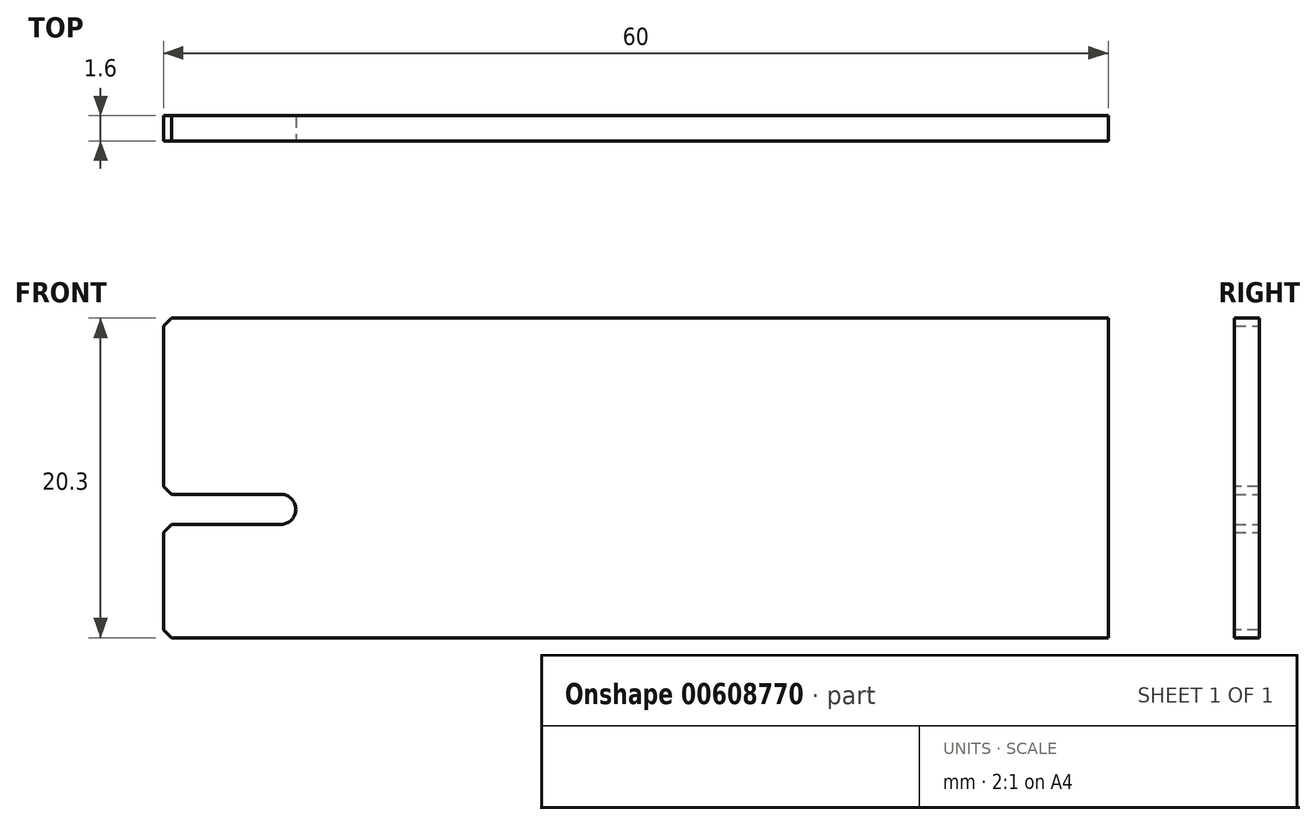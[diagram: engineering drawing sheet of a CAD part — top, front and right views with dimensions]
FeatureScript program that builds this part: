
annotation { "Feature Type Name" : "Feature", "Feature Type Description" : "" }
export const myFeature = defineFeature(function(context is Context, id is Id, definition is map)
    precondition{}
    {
        {
            var Q0;
            Q0=qCreatedBy(makeId("Front.planeOp"),FACE);
            var sketch = newSketch(context, id + "F0", { "sketchPlane" : qUnion([Q0])});
            skLineSegment(sketch, "E0.bottom", {"start": v(-10.18, 9.92) * mm, "end": v(49.82, 9.92) * mm});
            skLineSegment(sketch, "E0.top", {"start": v(-10.18, -10.38) * mm, "end": v(49.82, -10.38) * mm});
            skLineSegment(sketch, "E0.left", {"start": v(-10.18, 9.92) * mm, "end": v(-10.18, -10.38) * mm});
            skLineSegment(sketch, "E0.right", {"start": v(49.82, 9.92) * mm, "end": v(49.82, -10.38) * mm});
            skSolve(sketch);
        }
        {
            var Q0;
            Q0 = qSketchRegion(id + "F0", true);
            extrude(context, id + "F1", {"entities" : qUnion([Q0]), "depth" : 1.6 * mm, "offsetDistance" : 25 * mm});
        }
        {
            var Q0;
            Q0=qCreatedBy(makeId("Front.planeOp"),FACE);
            var sketch = newSketch(context, id + "F2", { "sketchPlane" : qUnion([Q0])});
            skLineSegment(sketch, "E1.bottom", {"start": v(-11.78, -1.28) * mm, "end": v(-1.78, -1.28) * mm});
            skLineSegment(sketch, "E1.top", {"start": v(-11.78, -3.18) * mm, "end": v(-1.78, -3.18) * mm});
            skLineSegment(sketch, "E1.left", {"start": v(-11.78, -1.28) * mm, "end": v(-11.78, -3.18) * mm});
            skLineSegment(sketch, "E1.right", {"start": v(-1.78, -1.28) * mm, "end": v(-1.78, -3.18) * mm});
            skSolve(sketch);
        }
        {
            var Q0;
            Q0 = qSketchRegion(id + "F2", true);
            extrude(context, id + "F3", {"entities" : qUnion([Q0]), "operationType" : NewBodyOperationType.REMOVE, "depth" : 25 * mm, "offsetDistance" : 25 * mm});
        }
        {
            var Q0;
            Q0=makeQuery(id+"F1.opExtrude","SWEPT_EDGE",EDGE,{"disambiguationData":[OSD([sQuery(id+"F0.wireOp",EDGE,"E0.bottom"),sQuery(id+"F0.wireOp",EDGE,"E0.left")])]});
            var Q1;
            Q1=makeQuery(id+"F3.boolean.opBoolean","INTERSECT",EDGE,{"derivedFrom":[makeQuery(id+"F1.opExtrude","SWEPT_FACE",FACE,{"disambiguationData":[OSD([sQuery(id+"F0.wireOp",EDGE,"E0.left")])]}),makeQuery(id+"F3.opExtrude","SWEPT_FACE",FACE,{"disambiguationData":[OSD([sQuery(id+"F2.wireOp",EDGE,"E1.bottom")])]})]});
            var Q2;
            Q2=makeQuery(id+"F3.boolean.opBoolean","INTERSECT",EDGE,{"derivedFrom":[makeQuery(id+"F1.opExtrude","SWEPT_FACE",FACE,{"disambiguationData":[OSD([sQuery(id+"F0.wireOp",EDGE,"E0.left")])]}),makeQuery(id+"F3.opExtrude","SWEPT_FACE",FACE,{"disambiguationData":[OSD([sQuery(id+"F2.wireOp",EDGE,"E1.top")])]})]});
            var Q3;
            Q3=makeQuery(id+"F1.opExtrude","SWEPT_EDGE",EDGE,{"disambiguationData":[OSD([sQuery(id+"F0.wireOp",EDGE,"E0.top"),sQuery(id+"F0.wireOp",EDGE,"E0.left")])]});
            chamfer(context, id + "F4", {"entities" : qUnion([Q0, Q1, Q2, Q3]), "width" : 0.5 * mm, "tangentPropagation" : true});
        }
        {
            var Q0;
            Q0=makeQuery(id+"F3.boolean.opBoolean","COPY",EDGE,{"derivedFrom":makeQuery(id+"F3.opExtrude","SWEPT_EDGE",EDGE,{"disambiguationData":[OSD([sQuery(id+"F2.wireOp",EDGE,"E1.bottom"),sQuery(id+"F2.wireOp",EDGE,"E1.right")])]})});
            var Q1;
            Q1=makeQuery(id+"F3.boolean.opBoolean","COPY",EDGE,{"derivedFrom":makeQuery(id+"F3.opExtrude","SWEPT_EDGE",EDGE,{"disambiguationData":[OSD([sQuery(id+"F2.wireOp",EDGE,"E1.top"),sQuery(id+"F2.wireOp",EDGE,"E1.right")])]})});
            fillet(context, id + "F5", {"entities" : qUnion([Q0, Q1]), "radius" : 0.95 * mm, "tangentPropagation" : true, "allowEdgeOverflow" : false});
        }
    });
